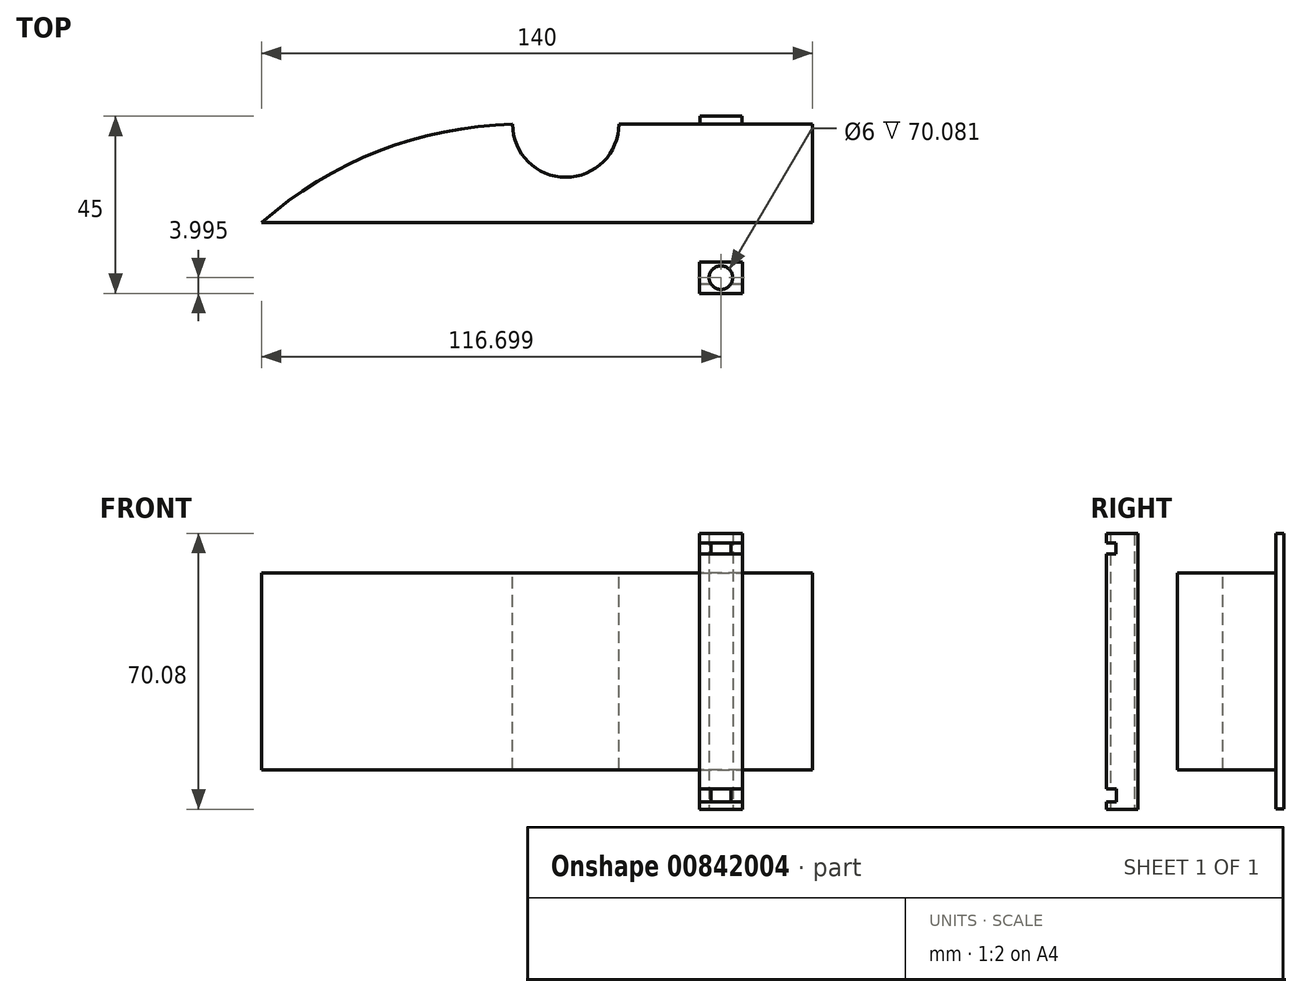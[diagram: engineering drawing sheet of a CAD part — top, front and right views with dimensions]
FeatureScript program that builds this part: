
annotation { "Feature Type Name" : "Feature", "Feature Type Description" : "" }
export const myFeature = defineFeature(function(context is Context, id is Id, definition is map)
    precondition{}
    {
        {
            var Q0;
            Q0=qCreatedBy(makeId("Top.planeOp"),FACE);
            var sketch = newSketch(context, id + "F0", { "sketchPlane" : qUnion([Q0])});
            skLineSegment(sketch, "E0", {"start": v(-71.6, -34.26) * mm, "end": v(68.4, -34.26) * mm});
            skLineSegment(sketch, "E1", {"start": v(68.4, -34.26) * mm, "end": v(68.4, -9.26) * mm});
            skLineSegment(sketch, "E2", {"start": v(68.4, -9.26) * mm, "end": v(-5.46, -9.26) * mm});
            skArc(sketch, "E3", {"start": v(-5.46, -9.26) * mm, "mid": v(-40.82, -15.72) * mm, "end": v(-71.6, -34.26) * mm});
            skSolve(sketch);
        }
        {
            var Q0;
            Q0=makeQuery(id+"F0.imprint","IMPRINT",FACE,{"disambiguationData":[TD([[makeQuery(id+"F0.imprint","IMPRINT",EDGE,{"derivedFrom":sQuery(id+"F0.wireOp",EDGE,"E0")}),1.0]])]});
            extrude(context, id + "F1", {"entities" : qUnion([Q0]), "depth" : 50 * mm, "offsetDistance" : 25.4 * mm});
        }
        {
            var Q0;
            Q0=makeQuery(id+"F1.opExtrude","CAP_FACE",FACE,{"disambiguationData":[OSD([sQuery(id+"F0.wireOp",EDGE,"E0"),sQuery(id+"F0.wireOp",EDGE,"E1"),sQuery(id+"F0.wireOp",EDGE,"E2"),sQuery(id+"F0.wireOp",EDGE,"E3")])],"isStart":false});
            var sketch = newSketch(context, id + "F2", { "sketchPlane" : qUnion([Q0])});
            skCircle(sketch, "E4", {"center": v(5.67, -9.26) * mm, "radius": 13.5 * mm});
            skSolve(sketch);
        }
        {
            var Q0;
            {var subQ0=sQuery(id+"F2.wireOp",EDGE,"E4");var subQ1=makeQuery(id+"F1.opExtrude","CAP_EDGE",EDGE,{"disambiguationData":[OSD([sQuery(id+"F0.wireOp",EDGE,"E2")])],"isStart":false});var subQ2=makeQuery(id+"F2.imprint","INTERSECT",VERTEX,{"derivedFrom":[subQ1,subQ0]});Q0=makeQuery(id+"F2.imprint","IMPRINT",FACE,{"disambiguationData":[TD([[makeQuery(id+"F2.imprint","IMPRINT",EDGE,{"disambiguationData":[TD([[subQ2,1.0]])],"derivedFrom":subQ0}),1.0]])]});}
            extrude(context, id + "F3", {"entities" : qUnion([Q0]), "operationType" : NewBodyOperationType.REMOVE, "oppositeDirection" : true, "depth" : 50 * mm, "offsetDistance" : 25 * mm});
        }
        {
            var Q0;
            Q0=makeQuery(id+"F1.opExtrude","SWEPT_FACE",FACE,{"disambiguationData":[OSD([sQuery(id+"F0.wireOp",EDGE,"E2")])]});
            var sketch = newSketch(context, id + "F4", { "sketchPlane" : qUnion([Q0])});
            skLineSegment(sketch, "E5", {"start": v(-50.37, 50) * mm, "end": v(-50.37, 60) * mm});
            skLineSegment(sketch, "E6", {"start": v(-50.37, 60) * mm, "end": v(-39.8, 60) * mm});
            skLineSegment(sketch, "E7", {"start": v(-39.8, 60) * mm, "end": v(-39.8, 50) * mm});
            skLineSegment(sketch, "E8", {"start": v(-39.8, 50) * mm, "end": v(-39.8, 0) * mm});
            skLineSegment(sketch, "E9", {"start": v(-39.8, 0) * mm, "end": v(-39.8, -10) * mm});
            skLineSegment(sketch, "E10", {"start": v(-39.8, -10) * mm, "end": v(-50.37, -10) * mm});
            skLineSegment(sketch, "E11", {"start": v(-50.37, -10) * mm, "end": v(-50.37, 0) * mm});
            skLineSegment(sketch, "E12", {"start": v(-50.37, 0) * mm, "end": v(-50.37, 50) * mm});
            skSolve(sketch);
        }
        {
            var Q0;
            Q0 = qSketchRegion(id + "F4", true);
            extrude(context, id + "F5", {"entities" : qUnion([Q0]), "depth" : 2 * mm, "offsetDistance" : 25 * mm});
        }
        {
            var Q0;
            {var subQ0=sQuery(id+"F4.wireOp",EDGE,"E6");var subQ1=sQuery(id+"F4.wireOp",EDGE,"E12");var subQ2=sQuery(id+"F4.wireOp",EDGE,"E11");var subQ3=sQuery(id+"F4.wireOp",EDGE,"E5");var subQ5=sQuery(id+"F4.wireOp",EDGE,"E9");var subQ6=sQuery(id+"F4.wireOp",EDGE,"E8");var subQ7=sQuery(id+"F4.wireOp",EDGE,"E7");Q0=makeQuery(id+"F5.boolean.opBoolean","SPLIT",FACE,{"disambiguationData":[TD([makeQuery(id+"F5.opExtrude","SWEPT_FACE",FACE,{"disambiguationData":[OSD([subQ0])]})])],"derivedFrom":makeQuery(id+"F5.opExtrude","CAP_FACE",FACE,{"disambiguationData":[OSD([subQ3,subQ0,subQ7,subQ6,subQ5,sQuery(id+"F4.wireOp",EDGE,"E10"),subQ2,subQ1])],"isStart":true})});}
            var sketch = newSketch(context, id + "F6", { "sketchPlane" : qUnion([Q0])});
            skLineSegment(sketch, "E13.bottom", {"start": v(43.7, 53.62) * mm, "end": v(45.7, 53.62) * mm});
            skLineSegment(sketch, "E13.top", {"start": v(43.7, 55.76) * mm, "end": v(45.7, 55.76) * mm});
            skLineSegment(sketch, "E13.left", {"start": v(43.7, 53.62) * mm, "end": v(43.7, 55.76) * mm});
            skLineSegment(sketch, "E13.right", {"start": v(45.7, 53.62) * mm, "end": v(45.7, 55.76) * mm});
            skSolve(sketch);
        }
        {
            var Q0;
            Q0 = qSketchRegion(id + "F6", true);
            extrude(context, id + "F7", {"entities" : qUnion([Q0]), "depth" : 35 * mm, "offsetDistance" : 25 * mm});
        }
        {
            var Q0;
            Q0=makeQuery(id+"F7.opExtrude","CAP_FACE",FACE,{"disambiguationData":[OSD([sQuery(id+"F6.wireOp",EDGE,"E13.bottom"),sQuery(id+"F6.wireOp",EDGE,"E13.top"),sQuery(id+"F6.wireOp",EDGE,"E13.left"),sQuery(id+"F6.wireOp",EDGE,"E13.right")])],"isStart":false});
            var sketch = newSketch(context, id + "F8", { "sketchPlane" : qUnion([Q0])});
            skLineSegment(sketch, "E14.bottom", {"start": v(39.65, 60.04) * mm, "end": v(50.53, 60.04) * mm});
            skLineSegment(sketch, "E14.top", {"start": v(39.65, -10.04) * mm, "end": v(50.53, -10.04) * mm});
            skLineSegment(sketch, "E14.left", {"start": v(39.65, 60.04) * mm, "end": v(39.65, -10.04) * mm});
            skLineSegment(sketch, "E14.right", {"start": v(50.53, 60.04) * mm, "end": v(50.53, -10.04) * mm});
            skSolve(sketch);
        }
        {
            var Q0;
            Q0 = qSketchRegion(id + "F8", true);
            extrude(context, id + "F9", {"entities" : qUnion([Q0]), "depth" : 8 * mm, "offsetDistance" : 25 * mm});
        }
        {
            var Q0;
            Q0=makeQuery(id+"F9.opExtrude","SWEPT_FACE",FACE,{"disambiguationData":[OSD([sQuery(id+"F8.wireOp",EDGE,"E14.top")])]});
            var sketch = newSketch(context, id + "F10", { "sketchPlane" : qUnion([Q0])});
            skCircle(sketch, "E15", {"center": v(45.09, 48.26) * mm, "radius": 3 * mm});
            skPoint(sketch, "E15.centerSnap0", {"position": v(45.09, 44.26) * mm});
            skPoint(sketch, "E15.centerSnap1", {"position": v(50.53, 48.26) * mm});
            skSolve(sketch);
        }
        {
            var Q0;
            Q0 = qSketchRegion(id + "F10", true);
            extrude(context, id + "F11", {"entities" : qUnion([Q0]), "operationType" : NewBodyOperationType.REMOVE, "endBound" : BoundingType.THROUGH_ALL, "oppositeDirection" : true, "depth" : 100 * mm, "offsetDistance" : 25 * mm});
        }
        {
            var Q0;
            Q0=makeQuery(id+"F7.opExtrude","SWEPT_BODY",BODY,{"disambiguationData":[OSD([sQuery(id+"F6.wireOp",EDGE,"E13.bottom"),sQuery(id+"F6.wireOp",EDGE,"E13.top"),sQuery(id+"F6.wireOp",EDGE,"E13.left"),sQuery(id+"F6.wireOp",EDGE,"E13.right")])]});
            deleteBodies(context, id + "F12", {"entities" : qUnion([Q0])});
        }
        {
            var Q0;
            Q0=makeQuery(id+"F9.opExtrude","SWEPT_FACE",FACE,{"disambiguationData":[OSD([sQuery(id+"F8.wireOp",EDGE,"E14.right")])]});
            var sketch = newSketch(context, id + "F13", { "sketchPlane" : qUnion([Q0])});
            skLineSegment(sketch, "E16.bottom", {"start": v(-52.26, 57.65) * mm, "end": v(-49.92, 57.65) * mm});
            skLineSegment(sketch, "E16.top", {"start": v(-52.26, 54.87) * mm, "end": v(-49.92, 54.87) * mm});
            skLineSegment(sketch, "E16.left", {"start": v(-52.26, 57.65) * mm, "end": v(-52.26, 54.87) * mm});
            skLineSegment(sketch, "E16.right", {"start": v(-49.92, 57.65) * mm, "end": v(-49.92, 54.87) * mm});
            skPoint(sketch, "E17.oppositeSnap0", {"position": v(-49.92, 56.26) * mm});
            skLineSegment(sketch, "E17.bottom", {"start": v(-52.26, -8.61) * mm, "end": v(-49.92, -8.61) * mm});
            skLineSegment(sketch, "E17.top", {"start": v(-52.26, -5.46) * mm, "end": v(-49.92, -5.46) * mm});
            skLineSegment(sketch, "E17.left", {"start": v(-52.26, -8.61) * mm, "end": v(-52.26, -5.46) * mm});
            skLineSegment(sketch, "E17.right", {"start": v(-49.92, -8.61) * mm, "end": v(-49.92, -5.46) * mm});
            skSolve(sketch);
        }
        {
            var Q0;
            Q0=makeQuery(id+"F13.imprint","IMPRINT",FACE,{"disambiguationData":[TD([[makeQuery(id+"F13.imprint","IMPRINT",EDGE,{"derivedFrom":sQuery(id+"F13.wireOp",EDGE,"E16.bottom")}),-1.0]])]});
            extrude(context, id + "F14", {"entities" : qUnion([Q0]), "operationType" : NewBodyOperationType.REMOVE, "oppositeDirection" : true, "depth" : 25 * mm, "offsetDistance" : 25 * mm});
        }
        {
            var Q0;
            Q0=makeQuery(id+"F9.opExtrude","SWEPT_FACE",FACE,{"disambiguationData":[OSD([sQuery(id+"F8.wireOp",EDGE,"E14.right")])]});
            var sketch = newSketch(context, id + "F15", { "sketchPlane" : qUnion([Q0])});
            skLineSegment(sketch, "E18.bottom", {"start": v(-52.26, -4.89) * mm, "end": v(-49.81, -4.89) * mm});
            skLineSegment(sketch, "E18.top", {"start": v(-52.26, -8.13) * mm, "end": v(-49.81, -8.13) * mm});
            skLineSegment(sketch, "E18.left", {"start": v(-52.26, -4.89) * mm, "end": v(-52.26, -8.13) * mm});
            skLineSegment(sketch, "E18.right", {"start": v(-49.81, -4.89) * mm, "end": v(-49.81, -8.13) * mm});
            skSolve(sketch);
        }
        {
            var Q0;
            Q0=makeQuery(id+"F15.imprint","IMPRINT",FACE,{"disambiguationData":[TD([[makeQuery(id+"F15.imprint","IMPRINT",EDGE,{"derivedFrom":sQuery(id+"F15.wireOp",EDGE,"E18.bottom")}),-1.0]])]});
            extrude(context, id + "F16", {"entities" : qUnion([Q0]), "operationType" : NewBodyOperationType.REMOVE, "oppositeDirection" : true, "depth" : 25 * mm, "offsetDistance" : 25 * mm});
        }
    });
